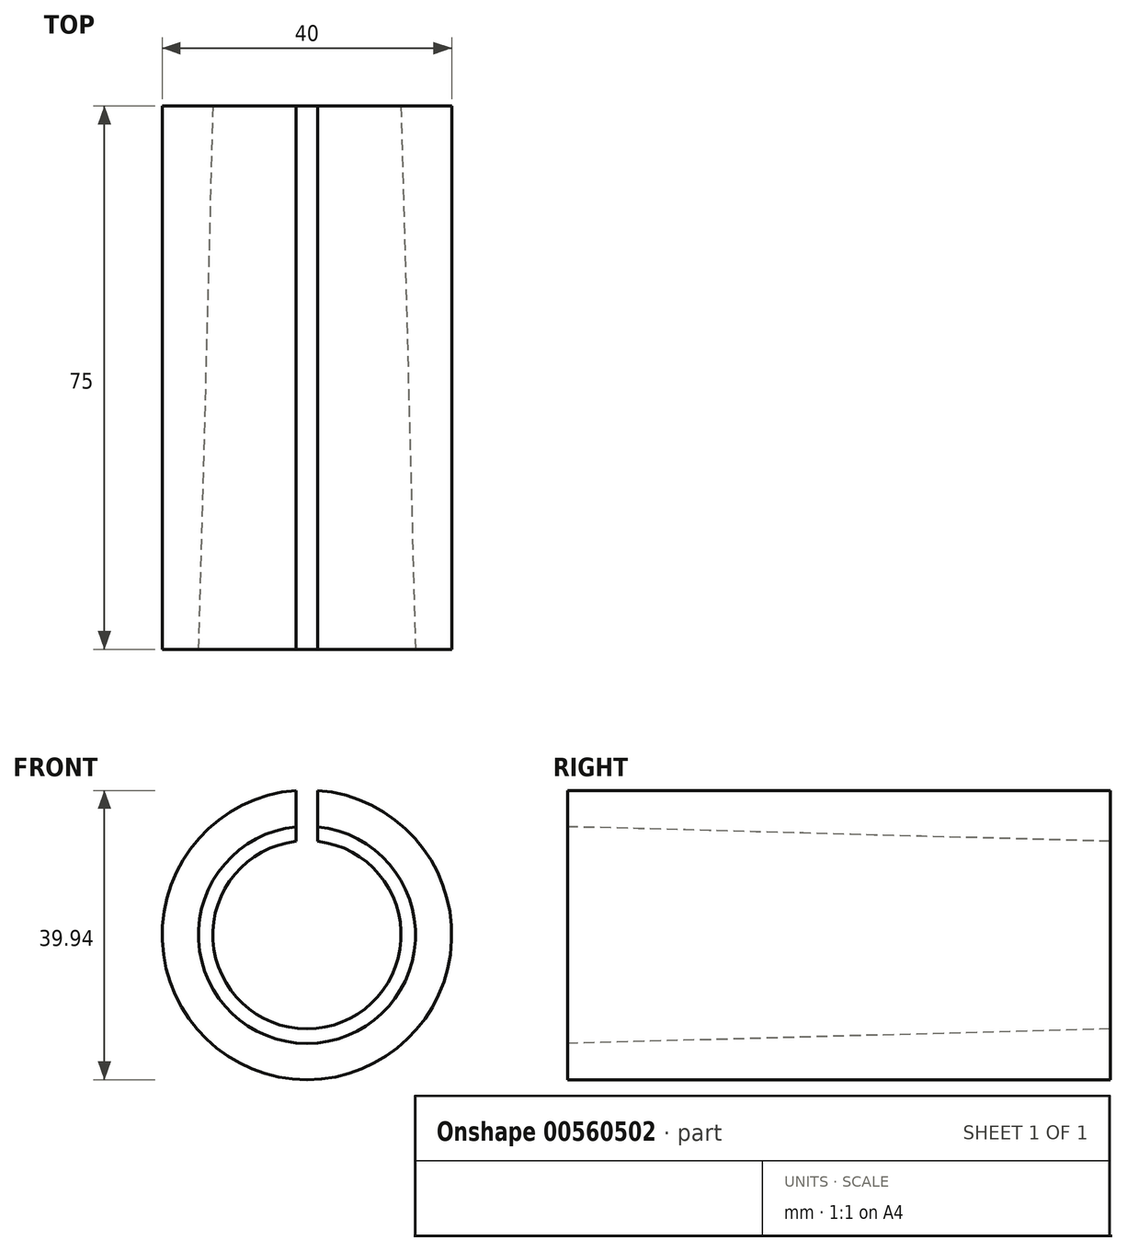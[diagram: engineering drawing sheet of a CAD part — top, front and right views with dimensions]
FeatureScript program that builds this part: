
annotation { "Feature Type Name" : "Feature", "Feature Type Description" : "" }
export const myFeature = defineFeature(function(context is Context, id is Id, definition is map)
    precondition{}
    {
        {
            var Q0;
            Q0=qCreatedBy(makeId("Front.planeOp"),FACE);
            var sketch = newSketch(context, id + "F0", { "sketchPlane" : qUnion([Q0])});
            skCircle(sketch, "E0", {"center": v(0, 0) * mm, "radius": 13 * mm});
            skCircle(sketch, "E1", {"center": v(0, 0) * mm, "radius": 20 * mm});
            skSolve(sketch);
        }
        {
            var Q0;
            Q0 = qSketchRegion(id + "F0", true);
            extrude(context, id + "F1", {"entities" : qUnion([Q0]), "depth" : 75 * mm, "offsetDistance" : 25 * mm});
        }
        {
            var Q0;
            Q0=qCreatedBy(makeId("Right.planeOp"),FACE);
            var sketch = newSketch(context, id + "F2", { "sketchPlane" : qUnion([Q0])});
            skLineSegment(sketch, "E2", {"start": v(-75, 15) * mm, "end": v(-75, 13) * mm});
            skLineSegment(sketch, "E3", {"start": v(-75, 13) * mm, "end": v(0, 13) * mm});
            skLineSegment(sketch, "E4", {"start": v(0, 13) * mm, "end": v(-75, 15) * mm});
            skSolve(sketch);
        }
        {
            var Q0;
            Q0 = qSketchRegion(id + "F2", true);
            var Q1;
            Q1=makeQuery(id+"F1.opExtrude","CAP_EDGE",EDGE,{"disambiguationData":[OSD([sQuery(id+"F0.wireOp",EDGE,"E0")])],"isStart":true});
            revolve(context, id + "F3", {"operationType" : NewBodyOperationType.REMOVE, "entities" : qUnion([Q0]), "axis" : qUnion([Q1]), "revolveType" : RevolveType.FULL, "oppositeDirection" : true});
        }
        {
            var Q0;
            Q0=makeQuery(id+"F1.opExtrude","CAP_FACE",FACE,{"disambiguationData":[OSD([sQuery(id+"F0.wireOp",EDGE,"E0"),sQuery(id+"F0.wireOp",EDGE,"E1")])],"isStart":true});
            var sketch = newSketch(context, id + "F4", { "sketchPlane" : qUnion([Q0])});
            skLineSegment(sketch, "E5.bottom", {"start": v(-1.5, 21) * mm, "end": v(1.5, 21) * mm});
            skLineSegment(sketch, "E5.top", {"start": v(-1.5, 12) * mm, "end": v(1.5, 12) * mm});
            skLineSegment(sketch, "E5.left", {"start": v(-1.5, 21) * mm, "end": v(-1.5, 12) * mm});
            skLineSegment(sketch, "E5.right", {"start": v(1.5, 21) * mm, "end": v(1.5, 12) * mm});
            skSolve(sketch);
        }
        {
            var Q0;
            Q0 = qSketchRegion(id + "F4", true);
            extrude(context, id + "F5", {"entities" : qUnion([Q0]), "operationType" : NewBodyOperationType.REMOVE, "oppositeDirection" : true, "depth" : 75 * mm, "offsetDistance" : 25 * mm});
        }
    });
